# Revit family: TD92_CLA040_BRA010_RVT20_R00
name_source: partatom
category: Mobiliário
units: mm (PartAtom-declared; Revit-internal decimal feet)

## family parameters
Com base no plano de trabalho = Não
Compartilhado = Não
Corte com vazios quando carregada = Não
Número OmniClass = 23.40.20.00
Ponto de cálculo do ambiente = Não
Sempre na vertical = Sim
Título OmniClass = General Furniture and Specialties

## types (1)
- TD92_CLA040_BRA010_RVT20_R00
    Descrição = Feita para decorar diferentes ambientes, a linha de cadeiras Clarice é sinônimo de inovação. Produzida com tecnologia de ponta a Cadeira Tramontina Clarice Branca com Braços em Polipropileno e Fibra de Vidro é leve, empilhável, resistente e com design diferenciado. É preferível que sua utilização seja em ambientes fechados, isso porque sua exposição prolongada ao sol pode aquecer a peça. Para evitar acidentes, não apoie-se nas duas pernas traseiras ou suba no assento. Submetida a rigorosos testes de qualidade, a cadeira resiste a uma carga estática de até 182 kg.
    Elevação padrão = 0  [stored 0 ft]
    Fabricante = Tramontina Delta S/A
    Modelo = Cadeira Tramontina Clarice Branca com Braços em Polipropileno e Fibra de Vidro
    Nota-chave = 92040010
    URL = https://www.tramontinastore.com

note: [stored X ft] marks values corroborated as IEEE doubles in the binary element streams (Revit-internal decimal feet)
